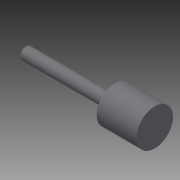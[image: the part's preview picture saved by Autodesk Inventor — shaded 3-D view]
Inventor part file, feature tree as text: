
AUTODESK INVENTOR PART (.ipt)
format: ipt  version: 2014 (Build 180170000, 170)  size: 119,808 bytes
history: native  units: in
note: dims shown in document units (in); Inventor stores cm internally (conversion verified against a paired STEP export)
features: other x49, revolve x2, sketch x2
ambient origin geometry x8: Origin, YZ Plane, XZ Plane, XY Plane, X Axis, Y Axis, Z Axis, Center Point
bodies: Solid1 (feature_tree)
feature tree (53):
  revolve  "Revolution1"  Angle=360.0deg
  revolve  "Revolution2"  [1 undecoded]
  other  "h1_XY"
  other  "h1_YZ"
  other  "h1_ZX"
  other  "h1_X"
  other  "h1_Y"
  other  "h1_Z"
  other  "h1_Center"
  other  "h2_XY"
  other  "h2_YZ"
  other  "h2_ZX"
  other  "h2_X"
  other  "h2_Y"
  other  "h2_Z"
  other  "h2_Center"
  other  "k1_XY"
  other  "k1_YZ"
  other  "k1_ZX"
  other  "k1_X"
  other  "k1_Y"
  other  "k1_Z"
  other  "k1_Center"
  other  "k2_XY"
  other  "k2_YZ"
  other  "k2_ZX"
  other  "k2_X"
  other  "k2_Y"
  other  "k2_Z"
  other  "k2_Center"
  other  "start_XY"
  other  "start_YZ"
  other  "start_ZX"
  other  "start_X"
  other  "start_Y"
  other  "start_Z"
  other  "start_Center"
  other  "to_prc_XY"
  other  "to_prc_YZ"
  other  "to_prc_ZX"
  other  "to_prc_X"
  other  "to_prc_Y"
  other  "to_prc_Z"
  other  "to_prc_Center"
  other  "to_rod_guide_XY"
  other  "to_rod_guide_YZ"
  other  "to_rod_guide_ZX"
  other  "to_rod_guide_X"
  other  "to_rod_guide_Y"
  other  "to_rod_guide_Z"
  other  "to_rod_guide_Center"
  sketch  "Sketch_5"  dims[d0=360.0deg d1=360.0deg]
  sketch  "Sketch_14"
note: 1 required parameter value undecoded (feature->parameter linkage not recoverable at this tier; creation-order binding heuristic only, values carry confidence <= 0.55)
